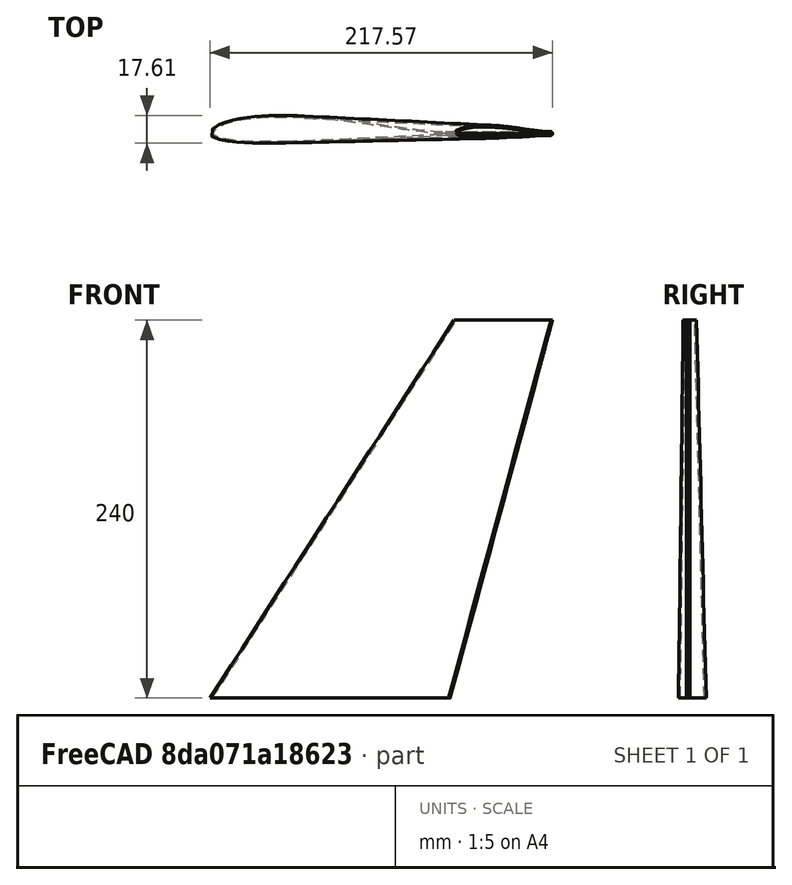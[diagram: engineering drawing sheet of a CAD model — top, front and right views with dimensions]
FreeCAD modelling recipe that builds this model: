
FCSTD DOCUMENT  (FreeCAD 1.0R39109 (Git))
Label: MH60 Airfoil Wing 25cm
License: All rights reserved
LicenseURL: https://en.wikipedia.org/wiki/All_rights_reserved
objects: Part::Part2DObjectPython×4, Sketcher::SketchObject×4, App::DocumentObjectGroup×1, PartDesign::AdditiveLoft×1, PartDesign::SubtractiveLoft×1, PartDesign::Thickness×1, PartDesign::Body×1
note: 22 computed .brp shape members not serialized (recipe doc carries the construction recipe); baked Part::Feature solids carry a one-line shape summary decoded from their .brp

FEATURE [Part::Part2DObjectPython] Wire  # Draft 2D object (typed FeaturePython)
  Area = 0.0628202
  ChamferSize = 0
  Closed = true
  End = (1,0,0)
  FilletRadius = 0
  Length = 2.02894
  MakeFace = true
  Points = (68) [(1,0,0),(0.996666,-0.00010721,0),(0.986577,-0.00021857,0),(0.969853,0.00016906,0),(0.94694,0.00139128,0),(0.918316,0.00361553,0),+62 more]
  Start = (1,0,0)
  Subdivisions = 0
FEATURE [App::DocumentObjectGroup] mh60
  Group = -> [Wire]
FEATURE [Part::Part2DObjectPython] BSpline  label="Original"  # Draft 2D object (typed FeaturePython)
  Area = 0.0629636
  Closed = true
  MakeFace = true
  Parameterization = 1
  Points = (67) [(1,0,0),(0.996666,-0.00010721,0),(0.986577,-0.00021857,0),(0.969853,0.00016906,0),(0.94694,0.00139128,0),(0.918316,0.00361553,0),+61 more]
FEATURE [Part::Part2DObjectPython] BSpline001  label="middePart15cm"  # Draft 2D object (typed FeaturePython)
  Area = 1416.68
  Closed = true
  MakeFace = true
  Parameterization = 1
  Points = (67) [(150,0,0),(149.5,-0.0160815,0),(147.987,-0.0327855,0),(145.478,0.025359,0),(142.041,0.208692,0),(137.747,0.54233,0),(132.685,1.05263,0),+60 more]
FEATURE [Part::Part2DObjectPython] BSpline002  label="externalPart6cm"  # Draft 2D object (typed FeaturePython)
  Area = 226.669
  Closed = true
  MakeFace = true
  Parameterization = 1
  Points = (67) [(60,0,0),(59.7999,-0.0064326,0),(59.1946,-0.0131142,0),(58.1912,0.0101436,0),(56.8164,0.0834768,0),(55.0989,0.216932,0),(53.0742,0.421051,0),+60 more]
FEATURE [Sketcher::SketchObject] Sketch
  ArcFitTolerance = 1e-06
  FullyConstrained = false
  MakeInternals = false
  sketch-geometry (137):
    g0: BSplineCurve PolesCount=68 KnotsCount=68 Degree=3 IsPeriodic=1
    g1-g68: Circle [constr] x68 (B-spline internal-alignment scaffolding for g0; pole/knot coordinates omitted)
    g69-g136: GeomPoint [constr] x68 (B-spline internal-alignment scaffolding for g0; pole/knot coordinates omitted)
  constraints (137):
    c: InternalAlignment(g1,g0)
    c: Weight(g1) = 1
    c: InternalAlignment(g2,g0)
    c: Equal(g2,g1)
    c: InternalAlignment(g3,g0)
    c: Equal(g3,g1)
    c: InternalAlignment(g4,g0)
    c: Equal(g4,g1)
    c: InternalAlignment(g5,g0)
    c: Equal(g5,g1)
    c: InternalAlignment(g6,g0)
    c: Equal(g6,g1)
    c: InternalAlignment(g7,g0)
    c: Equal(g7,g1)
    c: InternalAlignment(g8,g0)
    c: Equal(g8,g1)
    c: InternalAlignment(g9,g0)
    c: Equal(g9,g1)
    c: InternalAlignment(g10,g0)
    c: Equal(g10,g1)
    c: InternalAlignment(g11,g0)
    c: Equal(g11,g1)
    c: InternalAlignment(g12,g0)
    c: Equal(g12,g1)
    c: InternalAlignment(g13,g0)
    c: Equal(g13,g1)
    c: InternalAlignment(g14,g0)
    c: Equal(g14,g1)
    c: InternalAlignment(g15,g0)
    c: Equal(g15,g1)
    c: InternalAlignment(g16,g0)
    c: Equal(g16,g1)
    c: InternalAlignment(g17,g0)
    c: Equal(g17,g1)
    c: InternalAlignment(g18,g0)
    c: Equal(g18,g1)
    c: InternalAlignment(g19,g0)
    c: Equal(g19,g1)
    c: InternalAlignment(g20,g0)
    c: Equal(g20,g1)
    c: InternalAlignment(g21,g0)
    c: Equal(g21,g1)
    c: InternalAlignment(g22,g0)
    c: Equal(g22,g1)
    c: InternalAlignment(g23,g0)
    c: Equal(g23,g1)
    c: InternalAlignment(g24,g0)
    c: Equal(g24,g1)
    c: InternalAlignment(g25,g0)
    c: Equal(g25,g1)
    c: InternalAlignment(g26,g0)
    c: Equal(g26,g1)
    c: InternalAlignment(g27,g0)
    c: Equal(g27,g1)
    c: InternalAlignment(g28,g0)
    c: Equal(g28,g1)
    c: InternalAlignment(g29,g0)
    c: Equal(g29,g1)
    c: InternalAlignment(g30,g0)
    c: Equal(g30,g1)
    c: InternalAlignment(g31,g0)
    c: Equal(g31,g1)
    c: InternalAlignment(g32,g0)
    c: Equal(g32,g1)
    c: InternalAlignment(g33,g0)
    c: Equal(g33,g1)
    c: InternalAlignment(g34,g0)
    c: Equal(g34,g1)
    c: InternalAlignment(g35,g0)
    c: Equal(g35,g1)
    c: InternalAlignment(g36,g0)
    c: Equal(g36,g1)
    c: InternalAlignment(g37,g0)
    c: Equal(g37,g1)
    c: InternalAlignment(g38,g0)
    c: Equal(g38,g1)
    c: InternalAlignment(g39,g0)
    c: Equal(g39,g1)
    c: InternalAlignment(g40,g0)
    c: Equal(g40,g1)
    c: InternalAlignment(g41,g0)
    c: Equal(g41,g1)
    c: InternalAlignment(g42,g0)
    c: Equal(g42,g1)
    c: InternalAlignment(g43,g0)
    c: Equal(g43,g1)
    c: InternalAlignment(g44,g0)
    c: Equal(g44,g1)
    c: InternalAlignment(g45,g0)
    c: Equal(g45,g1)
    c: InternalAlignment(g46,g0)
    c: Equal(g46,g1)
    c: InternalAlignment(g47,g0)
    c: Equal(g47,g1)
    c: InternalAlignment(g48,g0)
    c: Equal(g48,g1)
    c: InternalAlignment(g49,g0)
    c: Equal(g49,g1)
    c: InternalAlignment(g50,g0)
    c: Equal(g50,g1)
    c: InternalAlignment(g51,g0)
    c: Equal(g51,g1)
    c: InternalAlignment(g52,g0)
    c: Equal(g52,g1)
    c: InternalAlignment(g53,g0)
    c: Equal(g53,g1)
    c: InternalAlignment(g54,g0)
    c: Equal(g54,g1)
    c: InternalAlignment(g55,g0)
    c: Equal(g55,g1)
    c: InternalAlignment(g56,g0)
    c: Equal(g56,g1)
    c: InternalAlignment(g57,g0)
    c: Equal(g57,g1)
    c: InternalAlignment(g58,g0)
    c: Equal(g58,g1)
    c: InternalAlignment(g59,g0)
    c: Equal(g59,g1)
    c: InternalAlignment(g60,g0)
    c: Equal(g60,g1)
    c: InternalAlignment(g61,g0)
    c: Equal(g61,g1)
    c: InternalAlignment(g62,g0)
    c: Equal(g62,g1)
    c: InternalAlignment(g63,g0)
    c: Equal(g63,g1)
    c: InternalAlignment(g64,g0)
    c: Equal(g64,g1)
    c: InternalAlignment(g65,g0)
    c: Equal(g65,g1)
    c: InternalAlignment(g66,g0)
    c: Equal(g66,g1)
    c: InternalAlignment(g67,g0)
    c: Equal(g67,g1)
    c: InternalAlignment(g68,g0)
    c: Equal(g68,g1)
    c: InternalAlignment(g69-g136 -> g0) x68
FEATURE [Sketcher::SketchObject] Sketch001
  ArcFitTolerance = 1e-06
  FullyConstrained = false
  MakeInternals = false
  Placement = pos=(155,0,240) rot=(0,0,1;0rad)
  sketch-geometry (137):
    g0: BSplineCurve PolesCount=68 KnotsCount=68 Degree=3 IsPeriodic=1
    g1-g68: Circle [constr] x68 (B-spline internal-alignment scaffolding for g0; pole/knot coordinates omitted)
    g69-g136: GeomPoint [constr] x68 (B-spline internal-alignment scaffolding for g0; pole/knot coordinates omitted)
  constraints (137):
    c: InternalAlignment(g1,g0)
    c: Weight(g1) = 1
    c: InternalAlignment(g2,g0)
    c: Equal(g2,g1)
    c: InternalAlignment(g3,g0)
    c: Equal(g3,g1)
    c: InternalAlignment(g4,g0)
    c: Equal(g4,g1)
    c: InternalAlignment(g5,g0)
    c: Equal(g5,g1)
    c: InternalAlignment(g6,g0)
    c: Equal(g6,g1)
    c: InternalAlignment(g7,g0)
    c: Equal(g7,g1)
    c: InternalAlignment(g8,g0)
    c: Equal(g8,g1)
    c: InternalAlignment(g9,g0)
    c: Equal(g9,g1)
    c: InternalAlignment(g10,g0)
    c: Equal(g10,g1)
    c: InternalAlignment(g11,g0)
    c: Equal(g11,g1)
    c: InternalAlignment(g12,g0)
    c: Equal(g12,g1)
    c: InternalAlignment(g13,g0)
    c: Equal(g13,g1)
    c: InternalAlignment(g14,g0)
    c: Equal(g14,g1)
    c: InternalAlignment(g15,g0)
    c: Equal(g15,g1)
    c: InternalAlignment(g16,g0)
    c: Equal(g16,g1)
    c: InternalAlignment(g17,g0)
    c: Equal(g17,g1)
    c: InternalAlignment(g18,g0)
    c: Equal(g18,g1)
    c: InternalAlignment(g19,g0)
    c: Equal(g19,g1)
    c: InternalAlignment(g20,g0)
    c: Equal(g20,g1)
    c: InternalAlignment(g21,g0)
    c: Equal(g21,g1)
    c: InternalAlignment(g22,g0)
    c: Equal(g22,g1)
    c: InternalAlignment(g23,g0)
    c: Equal(g23,g1)
    c: InternalAlignment(g24,g0)
    c: Equal(g24,g1)
    c: InternalAlignment(g25,g0)
    c: Equal(g25,g1)
    c: InternalAlignment(g26,g0)
    c: Equal(g26,g1)
    c: InternalAlignment(g27,g0)
    c: Equal(g27,g1)
    c: InternalAlignment(g28,g0)
    c: Equal(g28,g1)
    c: InternalAlignment(g29,g0)
    c: Equal(g29,g1)
    c: InternalAlignment(g30,g0)
    c: Equal(g30,g1)
    c: InternalAlignment(g31,g0)
    c: Equal(g31,g1)
    c: InternalAlignment(g32,g0)
    c: Equal(g32,g1)
    c: InternalAlignment(g33,g0)
    c: Equal(g33,g1)
    c: InternalAlignment(g34,g0)
    c: Equal(g34,g1)
    c: InternalAlignment(g35,g0)
    c: Equal(g35,g1)
    c: InternalAlignment(g36,g0)
    c: Equal(g36,g1)
    c: InternalAlignment(g37,g0)
    c: Equal(g37,g1)
    c: InternalAlignment(g38,g0)
    c: Equal(g38,g1)
    c: InternalAlignment(g39,g0)
    c: Equal(g39,g1)
    c: InternalAlignment(g40,g0)
    c: Equal(g40,g1)
    c: InternalAlignment(g41,g0)
    c: Equal(g41,g1)
    c: InternalAlignment(g42,g0)
    c: Equal(g42,g1)
    c: InternalAlignment(g43,g0)
    c: Equal(g43,g1)
    c: InternalAlignment(g44,g0)
    c: Equal(g44,g1)
    c: InternalAlignment(g45,g0)
    c: Equal(g45,g1)
    c: InternalAlignment(g46,g0)
    c: Equal(g46,g1)
    c: InternalAlignment(g47,g0)
    c: Equal(g47,g1)
    c: InternalAlignment(g48,g0)
    c: Equal(g48,g1)
    c: InternalAlignment(g49,g0)
    c: Equal(g49,g1)
    c: InternalAlignment(g50,g0)
    c: Equal(g50,g1)
    c: InternalAlignment(g51,g0)
    c: Equal(g51,g1)
    c: InternalAlignment(g52,g0)
    c: Equal(g52,g1)
    c: InternalAlignment(g53,g0)
    c: Equal(g53,g1)
    c: InternalAlignment(g54,g0)
    c: Equal(g54,g1)
    c: InternalAlignment(g55,g0)
    c: Equal(g55,g1)
    c: InternalAlignment(g56,g0)
    c: Equal(g56,g1)
    c: InternalAlignment(g57,g0)
    c: Equal(g57,g1)
    c: InternalAlignment(g58,g0)
    c: Equal(g58,g1)
    c: InternalAlignment(g59,g0)
    c: Equal(g59,g1)
    c: InternalAlignment(g60,g0)
    c: Equal(g60,g1)
    c: InternalAlignment(g61,g0)
    c: Equal(g61,g1)
    c: InternalAlignment(g62,g0)
    c: Equal(g62,g1)
    c: InternalAlignment(g63,g0)
    c: Equal(g63,g1)
    c: InternalAlignment(g64,g0)
    c: Equal(g64,g1)
    c: InternalAlignment(g65,g0)
    c: Equal(g65,g1)
    c: InternalAlignment(g66,g0)
    c: Equal(g66,g1)
    c: InternalAlignment(g67,g0)
    c: Equal(g67,g1)
    c: InternalAlignment(g68,g0)
    c: Equal(g68,g1)
    c: InternalAlignment(g69-g136 -> g0) x68
FEATURE [PartDesign::AdditiveLoft] AdditiveLoft
  Closed = false
  Profile = -> Sketch
  Refine = true
  Ruled = false
  Sections = -> [Sketch001]
  Suppressed = false
FEATURE [Sketcher::SketchObject] Sketch002
  ArcFitTolerance = 1e-06
  AttachmentSupport = -> [AdditiveLoft]
  FullyConstrained = true
  MakeInternals = false
  MapMode = 5
  Placement = pos=(0,0,0) rot=(1,0,0;3.14159rad)
  sketch-geometry (4):
    g0: LineSegment StartX=149.9 StartY=1 StartZ=0 EndX=149.9 EndY=-1 EndZ=0
    g1: LineSegment StartX=149.9 StartY=-1 StartZ=0 EndX=151.9 EndY=-1 EndZ=0
    g2: LineSegment StartX=151.9 StartY=-1 StartZ=0 EndX=151.9 EndY=1 EndZ=0
    g3: LineSegment StartX=151.9 StartY=1 StartZ=0 EndX=149.9 EndY=1 EndZ=0
  constraints (10):
    c: Coincident(g0,g1)
    c: Coincident(g1,g2)
    c: Coincident(g2,g3)
    c: Coincident(g3,g0)
    c: Horizontal(g1)
    c: DistanceX(g-1,g0) = 149.9
    c: Symmetric(g2,g1,g-1)
    c: Symmetric(g0,g0,g-1)
    c: Distance(g0,g0) = 2
    c: Distance(g1,g1) = 2
FEATURE [Sketcher::SketchObject] Sketch003
  ArcFitTolerance = 1e-06
  AttachmentSupport = -> [AdditiveLoft]
  FullyConstrained = true
  MakeInternals = false
  MapMode = 5
  Placement = pos=(0,0,240) rot=(0,0,1;0rad)
  sketch-geometry (4):
    g0: LineSegment StartX=214.9 StartY=1 StartZ=0 EndX=214.9 EndY=-1 EndZ=0
    g1: LineSegment StartX=214.9 StartY=-1 StartZ=0 EndX=216.9 EndY=-1 EndZ=0
    g2: LineSegment StartX=216.9 StartY=-1 StartZ=0 EndX=216.9 EndY=1 EndZ=0
    g3: LineSegment StartX=216.9 StartY=1 StartZ=0 EndX=214.9 EndY=1 EndZ=0
  constraints (10):
    c: Coincident(g0,g1)
    c: Coincident(g1,g2)
    c: Coincident(g2,g3)
    c: Coincident(g3,g0)
    c: Horizontal(g1)
    c: Symmetric(g2,g1,g-1)
    c: Symmetric(g0,g0,g-1)
    c: DistanceY(g0,g0) = 2
    c: Distance(g3,g3) = 2
    c: DistanceX(g-1,g0) = 214.9
FEATURE [PartDesign::SubtractiveLoft] SubtractiveLoft
  BaseFeature = -> AdditiveLoft
  Closed = false
  Profile = -> Sketch002
  Refine = true
  Ruled = false
  Sections = -> [Sketch003]
  Suppressed = false
FEATURE [PartDesign::Thickness] Thickness
  Base = -> SubtractiveLoft [Face4,Face1]
  BaseFeature = -> SubtractiveLoft
  Intersection = false
  Join = 0
  Mode = 0
  Refine = true
  SupportTransform = false
  Suppressed = false
  Value = 1.2
FEATURE [PartDesign::Body] Body
  AllowCompound = false
  Group = -> [Sketch,Sketch001,AdditiveLoft,Sketch002,Sketch003,SubtractiveLoft,Thickness]
  Origin = -> Origin
  Tip = -> Thickness
